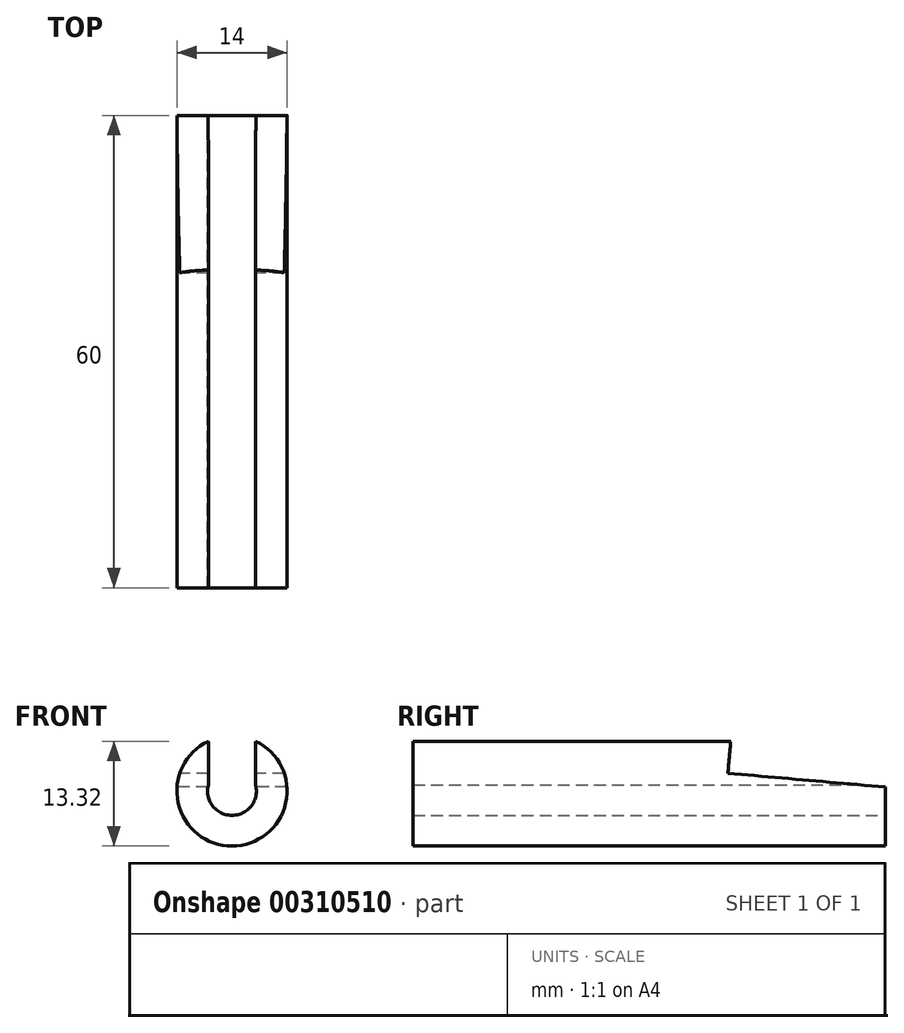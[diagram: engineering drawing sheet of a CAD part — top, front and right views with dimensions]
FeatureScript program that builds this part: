
annotation { "Feature Type Name" : "Feature", "Feature Type Description" : "" }
export const myFeature = defineFeature(function(context is Context, id is Id, definition is map)
    precondition{}
    {
        {
            var Q0;
            Q0=qCreatedBy(makeId("Front.planeOp"),FACE);
            var sketch = newSketch(context, id + "F0", { "sketchPlane" : qUnion([Q0])});
            skArc(sketch, "E0", {"start": v(-3, 6.32) * mm, "mid": v(0, -7) * mm, "end": v(3, 6.32) * mm});
            skArc(sketch, "E1", {"start": v(-3, 0.78) * mm, "mid": v(0, -3.1) * mm, "end": v(3, 0.78) * mm});
            skLineSegment(sketch, "E2.trimOffspring", {"start": v(-3, 0.78) * mm, "end": v(-3, 6.32) * mm});
            skLineSegment(sketch, "E3.trimOffspring", {"start": v(3, 0.78) * mm, "end": v(3, 6.32) * mm});
            skSolve(sketch);
        }
        {
            var Q0;
            Q0=makeQuery(id+"F0.imprint","IMPRINT",FACE,{"disambiguationData":[TD([[makeQuery(id+"F0.imprint","IMPRINT",EDGE,{"derivedFrom":sQuery(id+"F0.wireOp",EDGE,"E0")}),1.0]])]});
            var Q1;
            Q1 = qSketchRegion(id + "F2", true);
            extrude(context, id + "F1", {"entities" : qUnion([Q0, Q1]), "depth" : 60 * mm});
        }
        {
            var Q0;
            Q0=qCreatedBy(makeId("Right.planeOp"),FACE);
            var sketch = newSketch(context, id + "F2", { "sketchPlane" : qUnion([Q0])});
            skLineSegment(sketch, "E4", {"start": v(0, 0.5) * mm, "end": v(-20, 2.25) * mm});
            skLineSegment(sketch, "E5", {"start": v(0, 0.5) * mm, "end": v(0, 7.5) * mm});
            skLineSegment(sketch, "E6", {"start": v(-20, 2.25) * mm, "end": v(-19.54, 7.5) * mm});
            skLineSegment(sketch, "E7", {"start": v(0, 7.5) * mm, "end": v(-19.54, 7.5) * mm});
            skSolve(sketch);
        }
        {
            var Q0;
            Q0 = qSketchRegion(id + "F2", true);
            extrude(context, id + "F3", {"entities" : qUnion([Q0]), "operationType" : NewBodyOperationType.REMOVE, "depth" : 7 * mm, "hasSecondDirection" : true, "secondDirectionOppositeDirection" : true, "secondDirectionDepth" : 7 * mm});
        }
    });
